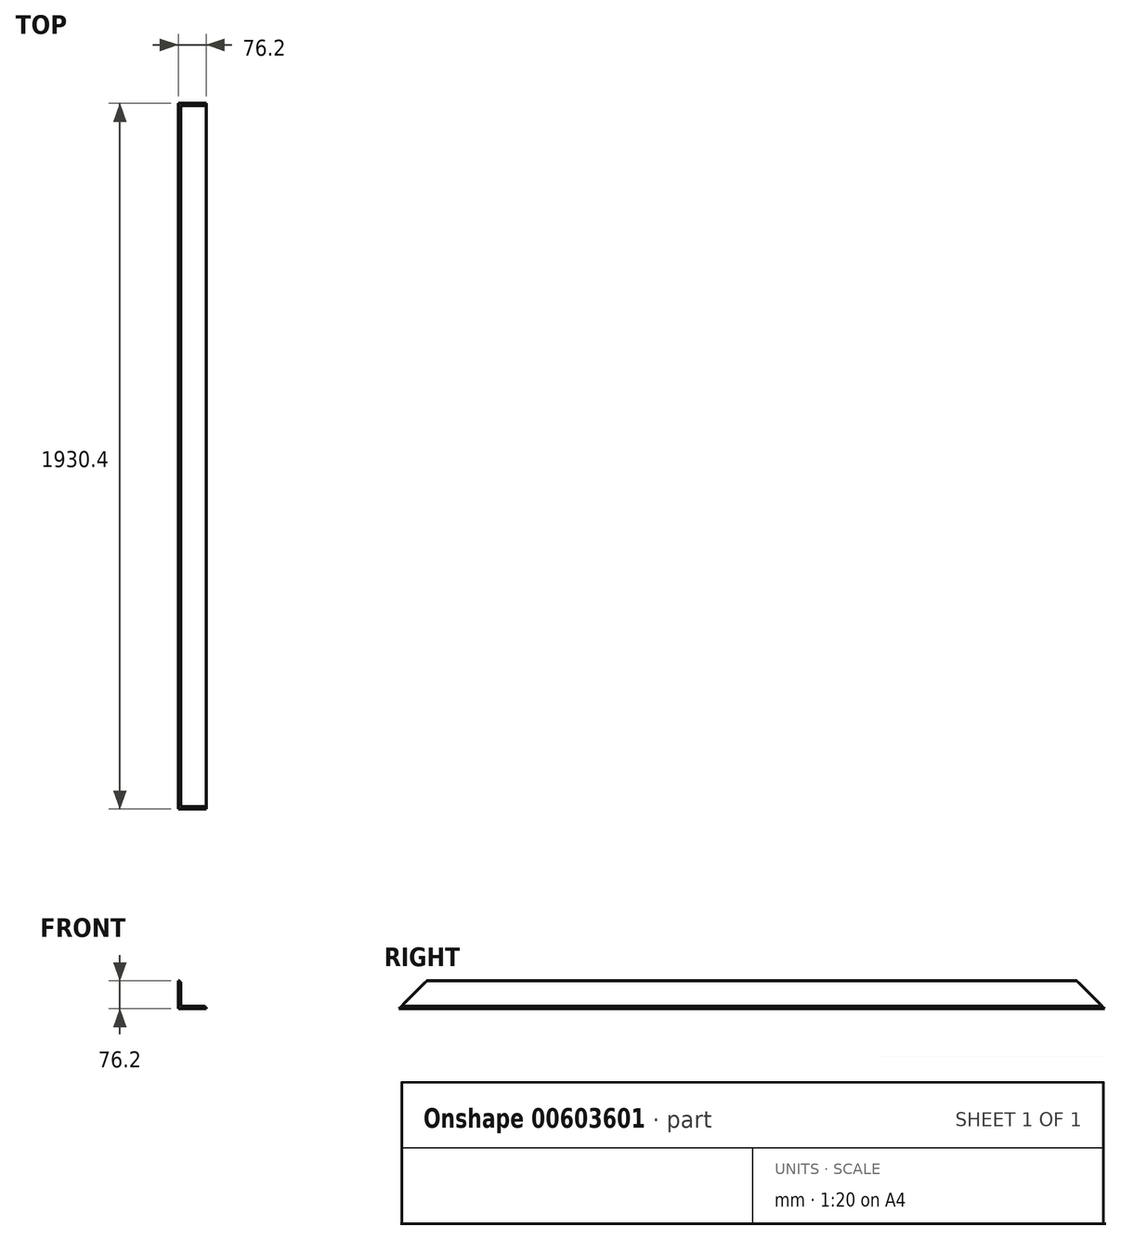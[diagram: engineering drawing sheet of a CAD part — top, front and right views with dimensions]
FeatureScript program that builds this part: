
annotation { "Feature Type Name" : "Feature", "Feature Type Description" : "" }
export const myFeature = defineFeature(function(context is Context, id is Id, definition is map)
    precondition{}
    {
        {
            var Q0;
            Q0=qCreatedBy(makeId("Front.planeOp"),FACE);
            var sketch = newSketch(context, id + "F0", { "sketchPlane" : qUnion([Q0])});
            skLineSegment(sketch, "E0.bottom", {"start": v(38.1, -38.1) * mm, "end": v(-38.1, -38.1) * mm});
            skLineSegment(sketch, "E0.top", {"start": v(-31.75, 38.1) * mm, "end": v(-38.1, 38.1) * mm});
            skLineSegment(sketch, "E0.left", {"start": v(38.1, -38.1) * mm, "end": v(38.1, -31.75) * mm});
            skLineSegment(sketch, "E0.right", {"start": v(-38.1, -38.1) * mm, "end": v(-38.1, 38.1) * mm});
            skPoint(sketch, "E0.middle", {"position": v(0, 0) * mm});
            skLineSegment(sketch, "E1.0", {"start": v(-31.75, -31.75) * mm, "end": v(-31.75, 38.1) * mm});
            skLineSegment(sketch, "E2.0", {"start": v(38.1, -31.75) * mm, "end": v(-31.75, -31.75) * mm});
            skPoint(sketch, "E3.orphan", {"position": v(38.1, 38.1) * mm});
            skSolve(sketch);
        }
        {
            var Q0;
            Q0 = qSketchRegion(id + "F0", true);
            extrude(context, id + "F1", {"entities" : qUnion([Q0]), "endBound" : BoundingType.SYMMETRIC, "depth" : 1930.4 * mm, "offsetDistance" : 25.4 * mm});
        }
        {
            var Q0;
            Q0=makeQuery(id+"F1.opExtrude","SWEPT_EDGE",EDGE,{"disambiguationData":[OSD([sQuery(id+"F0.wireOp",EDGE,"E0.top"),sQuery(id+"F0.wireOp",EDGE,"E1.0")])]});
            var Q1;
            Q1=makeQuery(id+"F1.opExtrude","SWEPT_EDGE",EDGE,{"disambiguationData":[OSD([sQuery(id+"F0.wireOp",EDGE,"E1.0"),sQuery(id+"F0.wireOp",EDGE,"E2.0")])]});
            var Q2;
            Q2=makeQuery(id+"F1.opExtrude","SWEPT_EDGE",EDGE,{"disambiguationData":[OSD([sQuery(id+"F0.wireOp",EDGE,"E0.left"),sQuery(id+"F0.wireOp",EDGE,"E2.0")])]});
            fillet(context, id + "F2", {"entities" : qUnion([Q0, Q1, Q2]), "radius" : 5.08 * mm, "tangentPropagation" : true, "allowEdgeOverflow" : false});
        }
        {
            var Q0;
            Q0=makeQuery(id+"F1.opExtrude","SWEPT_FACE",FACE,{"disambiguationData":[OSD([sQuery(id+"F0.wireOp",EDGE,"E0.right")])]});
            var sketch = newSketch(context, id + "F3", { "sketchPlane" : qUnion([Q0])});
            skPoint(sketch, "E4.0", {"position": v(-965.2, -38.1) * mm});
            skLineSegment(sketch, "E5", {"start": v(-965.2, -38.1) * mm, "end": v(-889, 38.1) * mm});
            skLineSegment(sketch, "E6", {"start": v(-889, 38.1) * mm, "end": v(-965.2, 38.1) * mm});
            skLineSegment(sketch, "E7", {"start": v(-965.2, 38.1) * mm, "end": v(-965.2, -38.1) * mm});
            skLineSegment(sketch, "E8.MirrorCS", {"start": v(965.2, -38.1) * mm, "end": v(889, 38.1) * mm});
            skLineSegment(sketch, "E9.MirrorCS", {"start": v(889, 38.1) * mm, "end": v(965.2, 38.1) * mm});
            skLineSegment(sketch, "E10.MirrorCS", {"start": v(965.2, 38.1) * mm, "end": v(965.2, -38.1) * mm});
            skSolve(sketch);
        }
        {
            var Q0;
            Q0 = qSketchRegion(id + "F3", true);
            extrude(context, id + "F4", {"entities" : qUnion([Q0]), "operationType" : NewBodyOperationType.REMOVE, "oppositeDirection" : true, "depth" : 76.2 * mm, "offsetDistance" : 25.4 * mm});
        }
    });
